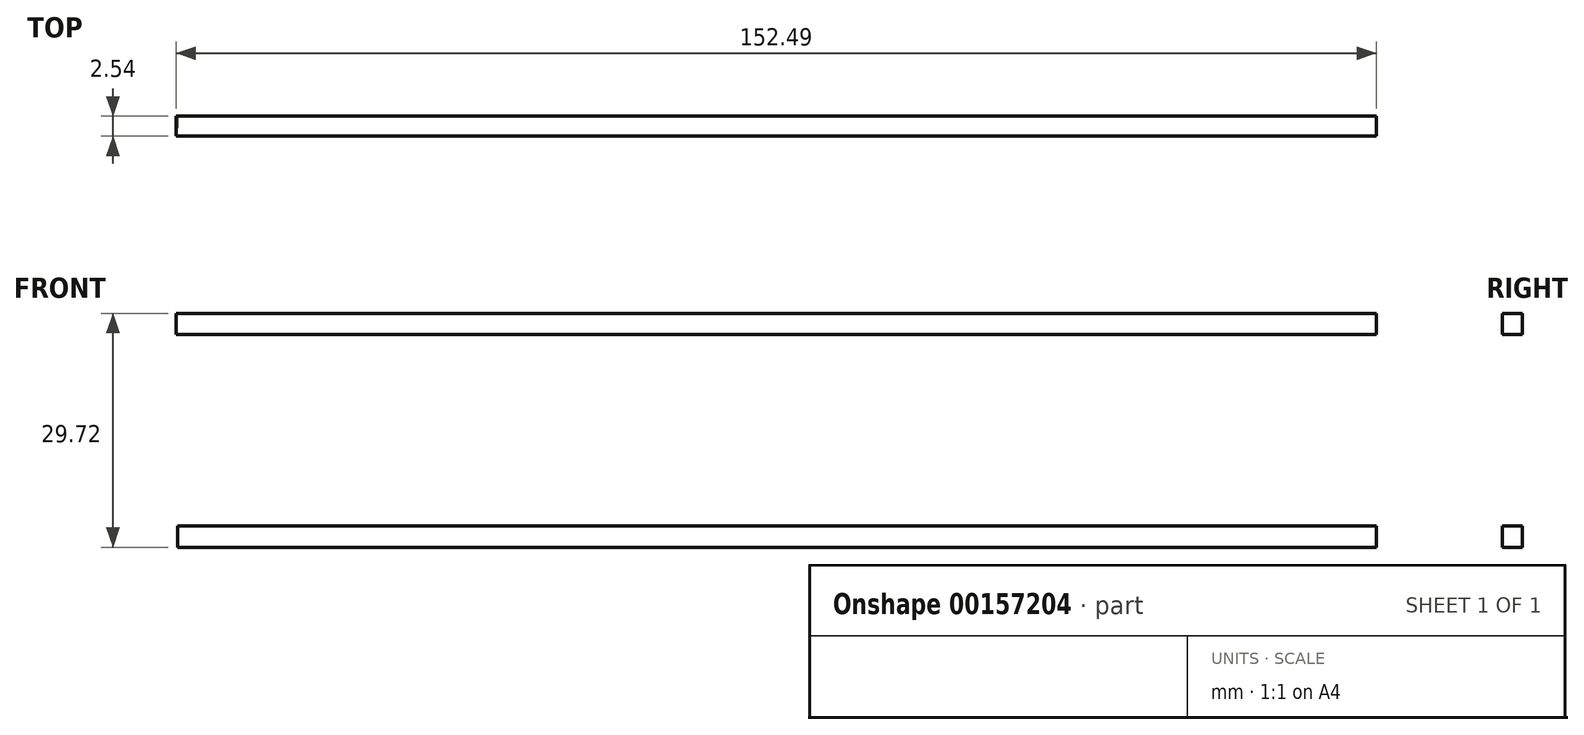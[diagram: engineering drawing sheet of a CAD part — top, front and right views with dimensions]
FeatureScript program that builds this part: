
annotation { "Feature Type Name" : "Feature", "Feature Type Description" : "" }
export const myFeature = defineFeature(function(context is Context, id is Id, definition is map)
    precondition{}
    {
        {
            var Q0;
            Q0=qCreatedBy(makeId("Front.planeOp"),FACE);
            var sketch = newSketch(context, id + "F0", { "sketchPlane" : qUnion([Q0])});
            skLineSegment(sketch, "E0.bottom", {"start": v(-76.25, -11.1) * mm, "end": v(76.05, -11.1) * mm});
            skLineSegment(sketch, "E0.top", {"start": v(-76.25, -13.8) * mm, "end": v(76.05, -13.8) * mm});
            skLineSegment(sketch, "E0.left", {"start": v(-76.25, -11.1) * mm, "end": v(-76.25, -13.8) * mm});
            skLineSegment(sketch, "E0.right", {"start": v(76.05, -11.1) * mm, "end": v(76.05, -13.8) * mm});
            skLineSegment(sketch, "E1.bottom", {"start": v(-76.44, 15.92) * mm, "end": v(76.05, 15.92) * mm});
            skLineSegment(sketch, "E1.top", {"start": v(-76.44, 13.22) * mm, "end": v(76.05, 13.22) * mm});
            skLineSegment(sketch, "E1.left", {"start": v(-76.44, 15.92) * mm, "end": v(-76.44, 13.22) * mm});
            skLineSegment(sketch, "E1.right", {"start": v(76.05, 15.92) * mm, "end": v(76.05, 13.22) * mm});
            skSolve(sketch);
        }
        {
            var Q0;
            Q0=makeQuery(id+"F0.imprint","IMPRINT",FACE,{"disambiguationData":[TD([[makeQuery(id+"F0.imprint","IMPRINT",EDGE,{"derivedFrom":sQuery(id+"F0.wireOp",EDGE,"E1.bottom")}),-1.0]])]});
            extrude(context, id + "F1", {"entities" : qUnion([Q0]), "oppositeDirection" : true, "depth" : 2.54 * mm});
        }
        {
            var Q0;
            Q0 = qSketchRegion(id + "F0", true);
            extrude(context, id + "F2", {"entities" : qUnion([Q0]), "operationType" : NewBodyOperationType.ADD, "oppositeDirection" : true, "depth" : 2.54 * mm});
        }
    });
